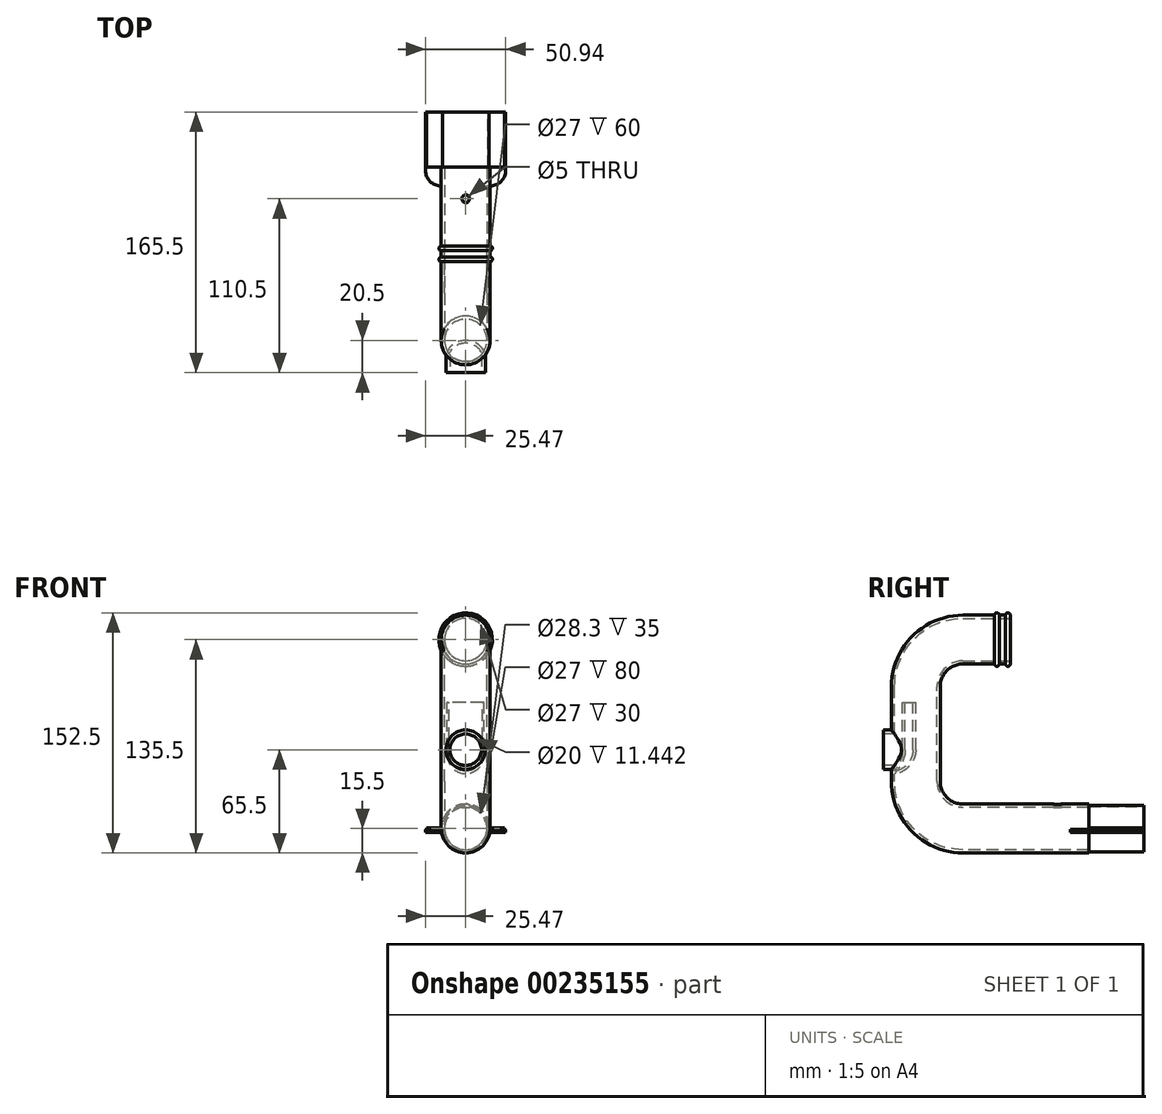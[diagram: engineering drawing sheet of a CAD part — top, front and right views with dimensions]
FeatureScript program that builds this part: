
annotation { "Feature Type Name" : "Feature", "Feature Type Description" : "" }
export const myFeature = defineFeature(function(context is Context, id is Id, definition is map)
    precondition{}
    {
        {
            var Q0;
            Q0=qCreatedBy(makeId("Front.planeOp"),FACE);
            var sketch = newSketch(context, id + "F0", { "sketchPlane" : qUnion([Q0])});
            skCircle(sketch, "E0", {"center": v(0, 0) * mm, "radius": 14.15 * mm});
            skArc(sketch, "E1", {"start": v(14.74, 0.5) * mm, "mid": v(0, 14.75) * mm, "end": v(-14.74, 0.5) * mm});
            skLineSegment(sketch, "E2.bottom", {"start": v(24.74, 0.5) * mm, "end": v(14.74, 0.5) * mm});
            skLineSegment(sketch, "E2.top", {"start": v(24.74, -0.5) * mm, "end": v(14.74, -0.5) * mm});
            skLineSegment(sketch, "E2.left", {"start": v(24.74, 0.5) * mm, "end": v(24.74, -0.5) * mm});
            skLineSegment(sketch, "E3.bottom", {"start": v(-14.74, 0.5) * mm, "end": v(-24.74, 0.5) * mm});
            skLineSegment(sketch, "E3.top", {"start": v(-14.74, -0.5) * mm, "end": v(-24.74, -0.5) * mm});
            skLineSegment(sketch, "E3.right", {"start": v(-24.74, 0.5) * mm, "end": v(-24.74, -0.5) * mm});
            skPoint(sketch, "E4", {"position": v(24.74, 0) * mm});
            skPoint(sketch, "E5", {"position": v(-24.74, 0) * mm});
            skArc(sketch, "E6.trimOffspring", {"start": v(-14.74, -0.5) * mm, "mid": v(0, -14.75) * mm, "end": v(14.74, -0.5) * mm});
            skSolve(sketch);
        }
        {
            var Q0;
            Q0 = qSketchRegion(id + "F0", true);
            extrude(context, id + "F1", {"entities" : qUnion([Q0]), "endBound" : BoundingType.SYMMETRIC, "depth" : 35 * mm});
        }
        {
            var Q0;
            Q0=qCreatedBy(makeId("Right.planeOp"),FACE);
            var sketch = newSketch(context, id + "F2", { "sketchPlane" : qUnion([Q0])});
            skLineSegment(sketch, "E7", {"start": v(-17.5, 0) * mm, "end": v(-97.5, 0) * mm});
            skArc(sketch, "E8", {"start": v(-127.5, 30) * mm, "mid": v(-118.71, 8.79) * mm, "end": v(-97.5, 0) * mm});
            skLineSegment(sketch, "E9", {"start": v(-127.5, 30) * mm, "end": v(-127.5, 90) * mm});
            skArc(sketch, "E10", {"start": v(-97.5, 120) * mm, "mid": v(-118.71, 111.21) * mm, "end": v(-127.5, 90) * mm});
            skLineSegment(sketch, "E11", {"start": v(-97.5, 120) * mm, "end": v(-67.5, 120) * mm});
            skSolve(sketch);
        }
        {
            var Q0;
            Q0=makeQuery(id+"F1.opExtrude","CAP_FACE",FACE,{"disambiguationData":[OSD([sQuery(id+"F0.wireOp",EDGE,"E0"),sQuery(id+"F0.wireOp",EDGE,"E1"),sQuery(id+"F0.wireOp",EDGE,"E2.bottom"),sQuery(id+"F0.wireOp",EDGE,"E2.top"),sQuery(id+"F0.wireOp",EDGE,"E2.left"),sQuery(id+"F0.wireOp",EDGE,"E3.bottom"),sQuery(id+"F0.wireOp",EDGE,"E3.top"),sQuery(id+"F0.wireOp",EDGE,"E3.right"),sQuery(id+"F0.wireOp",EDGE,"E6.trimOffspring")])],"isStart":false});
            var sketch = newSketch(context, id + "F3", { "sketchPlane" : qUnion([Q0])});
            skCircle(sketch, "E12", {"center": v(0, 0) * mm, "radius": 15.5 * mm});
            skCircle(sketch, "E13", {"center": v(0, 0) * mm, "radius": 13.5 * mm});
            skSolve(sketch);
        }
        {
            var Q0;
            Q0 = qSketchRegion(id + "F3", true);
            var Q1;
            Q1=sQuery(id+"F2.wireOp",EDGE,"E7");
            var Q2;
            Q2=sQuery(id+"F2.wireOp",EDGE,"E8");
            var Q3;
            Q3=sQuery(id+"F2.wireOp",EDGE,"E9");
            var Q4;
            Q4=sQuery(id+"F2.wireOp",EDGE,"E10");
            var Q5;
            Q5=sQuery(id+"F2.wireOp",EDGE,"E11");
            sweep(context, id + "F4", {"profiles" : qUnion([Q0]), "path" : qUnion([Q1, Q2, Q3, Q4, Q5])});
        }
        {
            var Q0;
            Q0=qCreatedBy(makeId("Front.planeOp"),FACE);
            var Q1;
            Q1=sQuery(id+"F2.wireOp",VERTEX,"E9.start");
            cPlane(context, id + "F5", {"entities" : qUnion([Q0, Q1]), "cplaneType" : CPlaneType.PLANE_POINT, "offset" : 25 * mm, "width" : 150 * mm, "height" : 150 * mm});
        }
        {
            var Q0;
            Q0=qCreatedBy(id+"F5.planeOp",FACE);
            cPlane(context, id + "F6", {"entities" : qUnion([Q0]), "cplaneType" : CPlaneType.OFFSET, "offset" : (31 / 2) * mm, "width" : 150 * mm, "height" : 150 * mm});
        }
        {
            var Q0;
            Q0=qCreatedBy(id+"F6.planeOp",FACE);
            cPlane(context, id + "F7", {"entities" : qUnion([Q0]), "cplaneType" : CPlaneType.OFFSET, "offset" : 5 * mm, "width" : 150 * mm, "height" : 150 * mm});
        }
        {
            var Q0;
            Q0=makeQuery(id+"F4.opSweep","CAP_FACE",FACE,{"disambiguationData":[OSD([sQuery(id+"F2.wireOp",VERTEX,"E11.end"),sQuery(id+"F3.wireOp",EDGE,"E12"),sQuery(id+"F3.wireOp",EDGE,"E13")])],"isStart":false});
            var sketch = newSketch(context, id + "F8", { "sketchPlane" : qUnion([Q0])});
            skPoint(sketch, "E14", {"position": v(0, 135.5) * mm});
            skSolve(sketch);
        }
        {
            var Q0;
            Q0=qCreatedBy(makeId("Right.planeOp"),FACE);
            var sketch = newSketch(context, id + "F9", { "sketchPlane" : qUnion([Q0])});
            skLineSegment(sketch, "E15.bottom", {"start": v(-67.5, 135.5) * mm, "end": v(-70.5, 135.5) * mm});
            skArc(sketch, "E16", {"start": v(-67.5, 135.5) * mm, "mid": v(-69, 137) * mm, "end": v(-70.5, 135.5) * mm});
            skArc(sketch, "E17", {"start": v(-74.5, 135.5) * mm, "mid": v(-76, 137) * mm, "end": v(-77.5, 135.5) * mm});
            skLineSegment(sketch, "E18", {"start": v(-77.5, 135.5) * mm, "end": v(-74.5, 135.5) * mm});
            skSolve(sketch);
        }
        {
            var Q0;
            Q0 = qSketchRegion(id + "F9", true);
            var Q1;
            Q1=sQuery(id+"F2.wireOp",EDGE,"E11");
            revolve(context, id + "F10", {"operationType" : NewBodyOperationType.ADD, "entities" : qUnion([Q0]), "axis" : qUnion([Q1]), "revolveType" : RevolveType.FULL});
        }
        {
            var Q0;
            Q0=qCreatedBy(makeId("Top.planeOp"),FACE);
            var sketch = newSketch(context, id + "F11", { "sketchPlane" : qUnion([Q0])});
            skCircle(sketch, "E19", {"center": v(0, -37.5) * mm, "radius": 2.5 * mm});
            skSolve(sketch);
        }
        {
            var Q0;
            Q0 = qSketchRegion(id + "F11", true);
            extrude(context, id + "F12", {"entities" : qUnion([Q0]), "operationType" : NewBodyOperationType.REMOVE, "endBound" : BoundingType.THROUGH_ALL, "depth" : 25 * mm});
        }
        {
            var Q0;
            Q0=qCreatedBy(makeId("Top.planeOp"),FACE);
            var Q1;
            Q1=sQuery(id+"F2.wireOp",VERTEX,"E10.center");
            cPlane(context, id + "F13", {"entities" : qUnion([Q0, Q1]), "cplaneType" : CPlaneType.PLANE_POINT, "offset" : 25 * mm, "width" : 150 * mm, "height" : 150 * mm});
        }
        {
            var Q0;
            Q0=qCreatedBy(id+"F13.planeOp",FACE);
            cPlane(context, id + "F14", {"entities" : qUnion([Q0]), "cplaneType" : CPlaneType.OFFSET, "offset" : 10 * mm, "oppositeDirection" : true, "width" : 150 * mm, "height" : 150 * mm});
        }
        {
            var Q0;
            Q0=makeQuery(id+"F1.opExtrude","CAP_FACE",FACE,{"disambiguationData":[OSD([sQuery(id+"F0.wireOp",EDGE,"E0"),sQuery(id+"F0.wireOp",EDGE,"E1"),sQuery(id+"F0.wireOp",EDGE,"E2.bottom"),sQuery(id+"F0.wireOp",EDGE,"E2.top"),sQuery(id+"F0.wireOp",EDGE,"E2.left"),sQuery(id+"F0.wireOp",EDGE,"E3.bottom"),sQuery(id+"F0.wireOp",EDGE,"E3.top"),sQuery(id+"F0.wireOp",EDGE,"E3.right"),sQuery(id+"F0.wireOp",EDGE,"E6.trimOffspring")])],"isStart":false});
            var sketch = newSketch(context, id + "F15", { "sketchPlane" : qUnion([Q0])});
            skSolve(sketch);
        }
        {
            var Q0;
            Q0=makeQuery(id+"F1.opExtrude","SWEPT_FACE",FACE,{"disambiguationData":[OSD([sQuery(id+"F0.wireOp",EDGE,"E3.top")])]});
            cPlane(context, id + "F16", {"entities" : qUnion([Q0]), "cplaneType" : CPlaneType.OFFSET, "offset" : 0 * mm, "width" : 150 * mm, "height" : 150 * mm});
        }
        {
            var Q0;
            Q0=qCreatedBy(id+"F16.planeOp",FACE);
            var sketch = newSketch(context, id + "F17", { "sketchPlane" : qUnion([Q0])});
            skLineSegment(sketch, "E20.bottom", {"start": v(-25.47, -17.5) * mm, "end": v(-14.85, -17.5) * mm});
            skLineSegment(sketch, "E20.top", {"start": v(-15.47, 29.43) * mm, "end": v(-14.85, 29.43) * mm});
            skLineSegment(sketch, "E20.left", {"start": v(-25.47, -17.5) * mm, "end": v(-25.47, 19.43) * mm});
            skPoint(sketch, "E20.middle", {"position": v(-20.16, 5.96) * mm});
            skPoint(sketch, "E21.middle", {"position": v(-14.85, 29.43) * mm});
            skPoint(sketch, "E22.visualSharp", {"position": v(-25.47, 29.43) * mm});
            skArc(sketch, "E22.filletArc", {"start": v(-15.47, 29.43) * mm, "mid": v(-22.54, 26.5) * mm, "end": v(-25.47, 19.43) * mm});
            skLineSegment(sketch, "E23", {"start": v(-14.85, 29.43) * mm, "end": v(-14.52, 29.43) * mm});
            skLineSegment(sketch, "E24", {"start": v(-14.52, 29.43) * mm, "end": v(-14.52, 17.5) * mm});
            skLineSegment(sketch, "E25", {"start": v(-14.52, 17.5) * mm, "end": v(-14.85, 17.5) * mm});
            skLineSegment(sketch, "E26", {"start": v(-14.85, 17.5) * mm, "end": v(-14.85, 17.5) * mm});
            skLineSegment(sketch, "E27", {"start": v(-14.85, 17.5) * mm, "end": v(-14.85, -17.5) * mm});
            skLineSegment(sketch, "E28.MirrorCS", {"start": v(14.52, 17.5) * mm, "end": v(14.85, 17.5) * mm});
            skLineSegment(sketch, "E29.MirrorCS", {"start": v(14.85, 29.43) * mm, "end": v(14.52, 29.43) * mm});
            skLineSegment(sketch, "E30.MirrorCS", {"start": v(15.47, 29.43) * mm, "end": v(14.85, 29.43) * mm});
            skPoint(sketch, "E31.MirrorP", {"position": v(25.47, 29.43) * mm});
            skPoint(sketch, "E32.MirrorP", {"position": v(14.85, 29.43) * mm});
            skArc(sketch, "E33.MirrorCS", {"start": v(15.47, 29.43) * mm, "mid": v(22.54, 26.5) * mm, "end": v(25.47, 19.43) * mm});
            skLineSegment(sketch, "E34.MirrorCS", {"start": v(25.47, -17.5) * mm, "end": v(14.85, -17.5) * mm});
            skLineSegment(sketch, "E35.MirrorCS", {"start": v(25.47, -17.5) * mm, "end": v(25.47, 19.43) * mm});
            skLineSegment(sketch, "E36.MirrorCS", {"start": v(14.85, 17.5) * mm, "end": v(14.85, -17.5) * mm});
            skLineSegment(sketch, "E37.MirrorCS", {"start": v(14.52, 29.43) * mm, "end": v(14.52, 17.5) * mm});
            skPoint(sketch, "E38.MirrorP", {"position": v(20.16, 5.96) * mm});
            skSolve(sketch);
        }
        {
            var Q0;
            Q0=makeQuery(id+"F17.imprint","IMPRINT",FACE,{"disambiguationData":[TD([[makeQuery(id+"F17.imprint","IMPRINT",EDGE,{"derivedFrom":sQuery(id+"F17.wireOp",EDGE,"E20.bottom")}),1.0]])]});
            var Q1;
            Q1=makeQuery(id+"F17.imprint","IMPRINT",FACE,{"disambiguationData":[TD([[makeQuery(id+"F17.imprint","IMPRINT",EDGE,{"derivedFrom":sQuery(id+"F17.wireOp",EDGE,"E28.MirrorCS")}),1.0]])]});
            extrude(context, id + "F18", {"entities" : qUnion([Q0, Q1]), "operationType" : NewBodyOperationType.ADD, "depth" : 2 * mm});
        }
        {
            var Q0;
            Q0=qCreatedBy(id+"F14.planeOp",FACE);
            var sketch = newSketch(context, id + "F19", { "sketchPlane" : qUnion([Q0])});
            skArc(sketch, "E39", {"start": v(11.7, -134.25) * mm, "mid": v(0, -127.5) * mm, "end": v(-11.7, -134.25) * mm});
            skArc(sketch, "E40", {"start": v(10.58, -135.89) * mm, "mid": v(0, -129.25) * mm, "end": v(-10.58, -135.89) * mm});
            skArc(sketch, "E41", {"start": v(-11.7, -134.25) * mm, "mid": v(-11.17, -135.09) * mm, "end": v(-10.58, -135.89) * mm});
            skArc(sketch, "E42.trimOffspring", {"start": v(10.58, -135.89) * mm, "mid": v(11.17, -135.09) * mm, "end": v(11.7, -134.25) * mm});
            skSolve(sketch);
        }
        {
            var Q0;
            Q0=qCreatedBy(id+"F7.planeOp",FACE);
            var sketch = newSketch(context, id + "F20", { "sketchPlane" : qUnion([Q0])});
            skCircle(sketch, "E43", {"center": v(0, 50) * mm, "radius": 12.5 * mm});
            skSolve(sketch);
        }
        {
            var Q0;
            Q0=qCreatedBy(id+"F7.planeOp",FACE);
            var sketch = newSketch(context, id + "F21", { "sketchPlane" : qUnion([Q0])});
            skPoint(sketch, "E44", {"position": v(0, 50) * mm});
            skSolve(sketch);
        }
        {
            var Q0;
            Q0=qCreatedBy(id+"F14.planeOp",FACE);
            var Q1;
            Q1=sQuery(id+"F21.wireOp",VERTEX,"E44");
            cPlane(context, id + "F22", {"entities" : qUnion([Q0, Q1]), "cplaneType" : CPlaneType.PLANE_POINT, "offset" : 25 * mm, "width" : 150 * mm, "height" : 150 * mm});
        }
        {
            var Q0;
            Q0 = qSketchRegion(id + "F19", true);
            var Q1;
            Q1=qCreatedBy(id+"F22.planeOp",FACE);
            extrude(context, id + "F23", {"entities" : qUnion([Q0]), "operationType" : NewBodyOperationType.ADD, "endBound" : BoundingType.UP_TO_SURFACE, "oppositeDirection" : true, "endBoundEntityFace" : qUnion([Q1]), "depth" : 25 * mm});
        }
        {
            var Q0;
            Q0=qCreatedBy(id+"F22.planeOp",FACE);
            var sketch = newSketch(context, id + "F24", { "sketchPlane" : qUnion([Q0])});
            skLineSegment(sketch, "E45", {"start": v(-47.98, -143) * mm, "end": v(51.28, -143) * mm, "construction": true});
            skSolve(sketch);
        }
        {
            var Q0;
            Q0=qCreatedBy(id+"F22.planeOp",FACE);
            var sketch = newSketch(context, id + "F25", { "sketchPlane" : qUnion([Q0])});
            skArc(sketch, "E46", {"start": v(11.7, -134.25) * mm, "mid": v(0, -127.5) * mm, "end": v(-11.7, -134.25) * mm});
            skArc(sketch, "E47", {"start": v(10.58, -135.89) * mm, "mid": v(0, -129.25) * mm, "end": v(-10.58, -135.89) * mm});
            skArc(sketch, "E48", {"start": v(-11.7, -134.25) * mm, "mid": v(-11.17, -135.09) * mm, "end": v(-10.58, -135.89) * mm});
            skArc(sketch, "E49.trimOffspring", {"start": v(10.58, -135.89) * mm, "mid": v(11.17, -135.09) * mm, "end": v(11.7, -134.25) * mm});
            skLineSegment(sketch, "E50", {"start": v(-47.91, -143) * mm, "end": v(49.06, -143) * mm, "construction": true});
            skSolve(sketch);
        }
        {
            var Q0;
            Q0 = qSketchRegion(id + "F25", true);
            var Q1;
            Q1=sQuery(id+"F25.wireOp",EDGE,"E50");
            revolve(context, id + "F26", {"operationType" : NewBodyOperationType.ADD, "entities" : qUnion([Q0]), "axis" : qUnion([Q1]), "revolveType" : RevolveType.ONE_DIRECTION, "oppositeDirection" : true, "angle" : 90 * degree});
        }
        {
            var Q0;
            Q0=qCreatedBy(makeId("Right.planeOp"),FACE);
            var sketch = newSketch(context, id + "F27", { "sketchPlane" : qUnion([Q0])});
            skLineSegment(sketch, "E51.bottom", {"start": v(-149.03, 90) * mm, "end": v(-143, 90) * mm});
            skLineSegment(sketch, "E51.top", {"start": v(-149.03, 33.52) * mm, "end": v(-143, 33.52) * mm});
            skLineSegment(sketch, "E51.left", {"start": v(-149.03, 90) * mm, "end": v(-149.03, 33.52) * mm});
            skLineSegment(sketch, "E51.right", {"start": v(-143, 90) * mm, "end": v(-143, 33.52) * mm});
            skPoint(sketch, "E51.middle", {"position": v(-146.01, 61.76) * mm});
            skSolve(sketch);
        }
        {
            var Q0;
            Q0 = qSketchRegion(id + "F27", true);
            var Q1;
            Q1=sQuery(id+"F2.wireOp",EDGE,"E9");
            revolve(context, id + "F28", {"operationType" : NewBodyOperationType.REMOVE, "entities" : qUnion([Q0]), "axis" : qUnion([Q1]), "revolveType" : RevolveType.FULL, "oppositeDirection" : true});
        }
        {
            var Q0;
            Q0 = qSketchRegion(id + "F20", true);
            extrude(context, id + "F29", {"entities" : qUnion([Q0]), "operationType" : NewBodyOperationType.ADD, "endBound" : BoundingType.UP_TO_NEXT, "oppositeDirection" : true, "depth" : 25 * mm});
        }
        {
            var Q0;
            Q0=makeQuery(id+"F29.opExtrude","CAP_FACE",FACE,{"disambiguationData":[OSD([sQuery(id+"F20.wireOp",EDGE,"E43")])],"isStart":true});
            var sketch = newSketch(context, id + "F30", { "sketchPlane" : qUnion([Q0])});
            skCircle(sketch, "E52", {"center": v(0, 50) * mm, "radius": 10 * mm});
            skSolve(sketch);
        }
        {
            var Q0;
            Q0 = qSketchRegion(id + "F30", true);
            extrude(context, id + "F31", {"entities" : qUnion([Q0]), "operationType" : NewBodyOperationType.REMOVE, "endBound" : BoundingType.UP_TO_NEXT, "oppositeDirection" : true, "depth" : 25 * mm});
        }
    });
